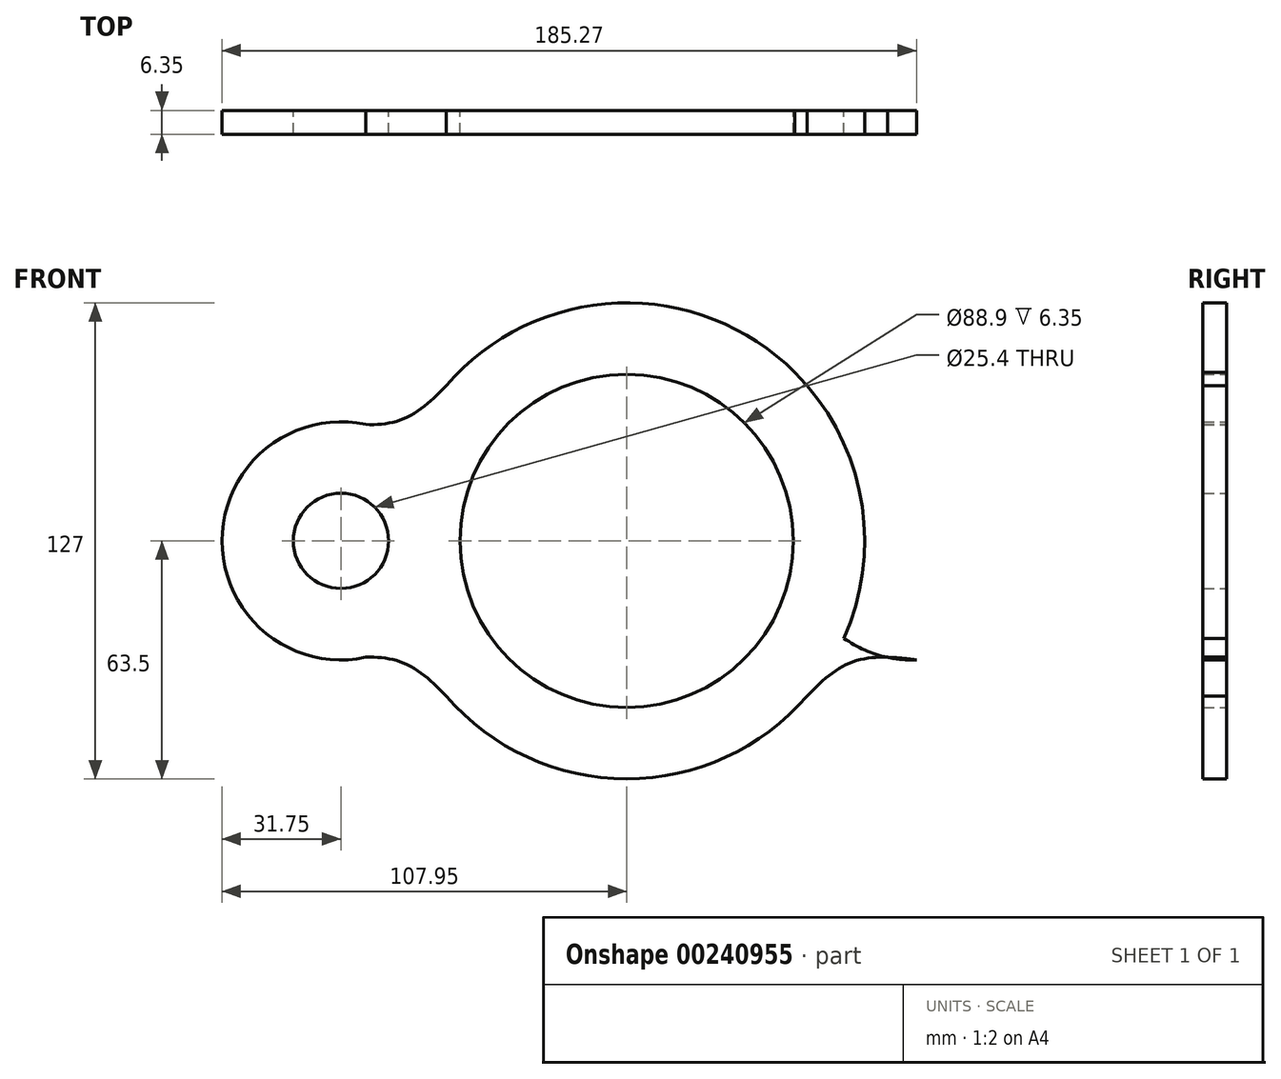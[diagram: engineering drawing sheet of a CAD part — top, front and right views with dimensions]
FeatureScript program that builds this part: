
annotation { "Feature Type Name" : "Feature", "Feature Type Description" : "" }
export const myFeature = defineFeature(function(context is Context, id is Id, definition is map)
    precondition{}
    {
        {
            var Q0;
            Q0=qCreatedBy(makeId("Front.planeOp"),FACE);
            var sketch = newSketch(context, id + "F0", { "sketchPlane" : qUnion([Q0])});
            skArc(sketch, "E0", {"start": v(0, 63.5) * mm, "mid": v(-44.9, 44.9) * mm, "end": v(-63.5, 0) * mm});
            skArc(sketch, "E1", {"start": v(-57.94, 25.98) * mm, "mid": v(-90.84, 28.18) * mm, "end": v(-107.95, 0) * mm});
            skFitSpline(sketch, "E2", {"points": [v(-44.9, 44.9) * mm, v(-60.08, 32.34) * mm, v(-77.32, 31.73) * mm], "startDerivative": vector(-27.75, -30.26) * mm, "endDerivative": vector(-37.2, 4.24) * mm});
            skFitSpline(sketch, "E3.MirrorCS", {"points": [v(-44.9, -44.9) * mm, v(-60.08, -32.34) * mm, v(-77.32, -31.73) * mm], "startDerivative": vector(-27.75, 30.26) * mm, "endDerivative": vector(-37.2, -4.24) * mm});
            skArc(sketch, "E4.MirrorCS", {"start": v(0, -63.5) * mm, "mid": v(-44.9, -44.9) * mm, "end": v(-63.5, 0) * mm});
            skArc(sketch, "E5.MirrorCS", {"start": v(-57.94, -25.98) * mm, "mid": v(-90.84, -28.18) * mm, "end": v(-107.95, 0) * mm});
            skArc(sketch, "E6.MirrorCS", {"start": v(0, 63.5) * mm, "mid": v(44.9, 44.9) * mm, "end": v(63.5, 0) * mm});
            skArc(sketch, "E7.MirrorCS", {"start": v(0, -63.5) * mm, "mid": v(44.9, -44.9) * mm, "end": v(63.5, 0) * mm});
            skArc(sketch, "E8.MirrorCS", {"start": v(57.94, -25.98) * mm, "mid": v(90.84, -28.18) * mm, "end": v(107.95, 0) * mm});
            skArc(sketch, "E9.MirrorCS", {"start": v(57.94, 25.98) * mm, "mid": v(90.84, 28.18) * mm, "end": v(107.95, 0) * mm});
            skFitSpline(sketch, "E10.MirrorCS", {"points": [v(44.9, 44.9) * mm, v(60.08, 32.34) * mm, v(77.32, 31.73) * mm], "startDerivative": vector(27.75, -30.26) * mm, "endDerivative": vector(37.2, 4.24) * mm});
            skFitSpline(sketch, "E11.MirrorCS", {"points": [v(44.9, -44.9) * mm, v(60.08, -32.34) * mm, v(77.32, -31.73) * mm], "startDerivative": vector(27.75, 30.26) * mm, "endDerivative": vector(37.2, -4.24) * mm});
            skCircle(sketch, "E12", {"center": v(0, 0) * mm, "radius": 44.45 * mm});
            skSolve(sketch);
        }
        {
            var Q0;
            {var subQ5=sQuery(id+"F0.wireOp",EDGE,"E7.MirrorCS");var subQ8=sQuery(id+"F0.wireOp",EDGE,"E6.MirrorCS");var subQ9=makeQuery(id+"F0.imprint","INTERSECT",VERTEX,{"derivedFrom":[subQ8,subQ5]});Q0=makeQuery(id+"F0.imprint","IMPRINT",FACE,{"disambiguationData":[TD([[makeQuery(id+"F0.imprint","IMPRINT",EDGE,{"disambiguationData":[TD([[subQ9,1.0]])],"derivedFrom":subQ8}),1.0]])]});}
            var Q1;
            {var subQ0=sQuery(id+"F0.wireOp",EDGE,"E4.MirrorCS");var subQ1=sQuery(id+"F0.wireOp",EDGE,"E3.MirrorCS");var subQ2=makeQuery(id+"F0.imprint","INTERSECT",VERTEX,{"disambiguationData":[OD(1.0)],"derivedFrom":[subQ1,subQ0]});Q1=makeQuery(id+"F0.imprint","IMPRINT",FACE,{"disambiguationData":[TD([[makeQuery(id+"F0.imprint","IMPRINT",EDGE,{"disambiguationData":[TD([[subQ2,-1.0]])],"derivedFrom":subQ1}),-1.0]])]});}
            var Q2;
            Q2=makeQuery(id+"F0.imprint","IMPRINT",FACE,{"disambiguationData":[TD([[makeQuery(id+"F0.imprint","IMPRINT",EDGE,{"derivedFrom":sQuery(id+"F0.wireOp",EDGE,"E12")}),1.0]])]});
            var Q3;
            {var subQ0=sQuery(id+"F0.wireOp",EDGE,"E9.MirrorCS");var subQ1=sQuery(id+"F0.wireOp",EDGE,"E6.MirrorCS");var subQ2=makeQuery(id+"F0.imprint","INTERSECT",VERTEX,{"derivedFrom":[subQ1,subQ0]});Q3=makeQuery(id+"F0.imprint","IMPRINT",FACE,{"disambiguationData":[TD([[makeQuery(id+"F0.imprint","IMPRINT",EDGE,{"disambiguationData":[TD([[subQ2,1.0]])],"derivedFrom":subQ1}),1.0]])]});}
            var Q4;
            {var subQ0=sQuery(id+"F0.wireOp",EDGE,"E8.MirrorCS");var subQ1=sQuery(id+"F0.wireOp",EDGE,"E7.MirrorCS");var subQ2=makeQuery(id+"F0.imprint","INTERSECT",VERTEX,{"derivedFrom":[subQ1,subQ0]});Q4=makeQuery(id+"F0.imprint","IMPRINT",FACE,{"disambiguationData":[TD([[makeQuery(id+"F0.imprint","IMPRINT",EDGE,{"disambiguationData":[TD([[subQ2,1.0]])],"derivedFrom":subQ1}),-1.0]])]});}
            var Q5;
            {var subQ0=sQuery(id+"F0.wireOp",EDGE,"E10.MirrorCS");var subQ1=sQuery(id+"F0.wireOp",EDGE,"E9.MirrorCS");var subQ2=makeQuery(id+"F0.imprint","INTERSECT",VERTEX,{"disambiguationData":[OD(0.0)],"derivedFrom":[subQ1,subQ0]});Q5=makeQuery(id+"F0.imprint","IMPRINT",FACE,{"disambiguationData":[TD([[makeQuery(id+"F0.imprint","IMPRINT",EDGE,{"disambiguationData":[TD([[subQ2,1.0]])],"derivedFrom":subQ1}),-1.0]])]});}
            var Q6;
            {var subQ0=sQuery(id+"F0.wireOp",EDGE,"E1");var subQ1=sQuery(id+"F0.wireOp",EDGE,"E0");var subQ2=makeQuery(id+"F0.imprint","INTERSECT",VERTEX,{"derivedFrom":[subQ1,subQ0]});Q6=makeQuery(id+"F0.imprint","IMPRINT",FACE,{"disambiguationData":[TD([[makeQuery(id+"F0.imprint","IMPRINT",EDGE,{"disambiguationData":[TD([[subQ2,1.0]])],"derivedFrom":subQ1}),-1.0]])]});}
            var Q7;
            {var subQ0=sQuery(id+"F0.wireOp",EDGE,"E5.MirrorCS");var subQ1=sQuery(id+"F0.wireOp",EDGE,"E3.MirrorCS");var subQ2=makeQuery(id+"F0.imprint","INTERSECT",VERTEX,{"disambiguationData":[OD(0.0)],"derivedFrom":[subQ1,subQ0]});Q7=makeQuery(id+"F0.imprint","IMPRINT",FACE,{"disambiguationData":[TD([[makeQuery(id+"F0.imprint","IMPRINT",EDGE,{"disambiguationData":[TD([[subQ2,1.0]])],"derivedFrom":subQ1}),1.0]])]});}
            var Q8;
            {var subQ0=sQuery(id+"F0.wireOp",EDGE,"E2");var subQ1=sQuery(id+"F0.wireOp",EDGE,"E0");var subQ2=makeQuery(id+"F0.imprint","INTERSECT",VERTEX,{"disambiguationData":[OD(0.0)],"derivedFrom":[subQ1,subQ0]});Q8=makeQuery(id+"F0.imprint","IMPRINT",FACE,{"disambiguationData":[TD([[makeQuery(id+"F0.imprint","IMPRINT",EDGE,{"disambiguationData":[TD([[subQ2,-1.0]])],"derivedFrom":subQ1}),1.0]])]});}
            var Q9;
            {var subQ0=sQuery(id+"F0.wireOp",EDGE,"E2");var subQ1=sQuery(id+"F0.wireOp",EDGE,"E1");var subQ2=makeQuery(id+"F0.imprint","INTERSECT",VERTEX,{"disambiguationData":[OD(0.0)],"derivedFrom":[subQ1,subQ0]});Q9=makeQuery(id+"F0.imprint","IMPRINT",FACE,{"disambiguationData":[TD([[makeQuery(id+"F0.imprint","IMPRINT",EDGE,{"disambiguationData":[TD([[subQ2,1.0]])],"derivedFrom":subQ1}),1.0]])]});}
            var Q10;
            {var subQ0=sQuery(id+"F0.wireOp",EDGE,"E11.MirrorCS");var subQ1=sQuery(id+"F0.wireOp",EDGE,"E7.MirrorCS");var subQ2=makeQuery(id+"F0.imprint","INTERSECT",VERTEX,{"disambiguationData":[OD(0.0)],"derivedFrom":[subQ1,subQ0]});Q10=makeQuery(id+"F0.imprint","IMPRINT",FACE,{"disambiguationData":[TD([[makeQuery(id+"F0.imprint","IMPRINT",EDGE,{"disambiguationData":[TD([[subQ2,-1.0]])],"derivedFrom":subQ1}),1.0]])]});}
            var Q11;
            {var subQ0=sQuery(id+"F0.wireOp",EDGE,"E10.MirrorCS");var subQ1=sQuery(id+"F0.wireOp",EDGE,"E6.MirrorCS");var subQ2=makeQuery(id+"F0.imprint","INTERSECT",VERTEX,{"disambiguationData":[OD(0.0)],"derivedFrom":[subQ1,subQ0]});Q11=makeQuery(id+"F0.imprint","IMPRINT",FACE,{"disambiguationData":[TD([[makeQuery(id+"F0.imprint","IMPRINT",EDGE,{"disambiguationData":[TD([[subQ2,-1.0]])],"derivedFrom":subQ1}),-1.0]])]});}
            var Q12;
            {var subQ0=sQuery(id+"F0.wireOp",EDGE,"E4.MirrorCS");var subQ1=sQuery(id+"F0.wireOp",EDGE,"E3.MirrorCS");var subQ2=makeQuery(id+"F0.imprint","INTERSECT",VERTEX,{"disambiguationData":[OD(0.0)],"derivedFrom":[subQ1,subQ0]});Q12=makeQuery(id+"F0.imprint","IMPRINT",FACE,{"disambiguationData":[TD([[makeQuery(id+"F0.imprint","IMPRINT",EDGE,{"disambiguationData":[TD([[subQ2,-1.0]])],"derivedFrom":subQ1}),1.0]])]});}
            var Q13;
            {var subQ0=sQuery(id+"F0.wireOp",EDGE,"E11.MirrorCS");var subQ1=sQuery(id+"F0.wireOp",EDGE,"E8.MirrorCS");var subQ2=makeQuery(id+"F0.imprint","INTERSECT",VERTEX,{"disambiguationData":[OD(0.0)],"derivedFrom":[subQ1,subQ0]});Q13=makeQuery(id+"F0.imprint","IMPRINT",FACE,{"disambiguationData":[TD([[makeQuery(id+"F0.imprint","IMPRINT",EDGE,{"disambiguationData":[TD([[subQ2,1.0]])],"derivedFrom":subQ1}),1.0]])]});}
            var Q14;
            Q14=makeQuery(id+"F0.imprint","IMPRINT",FACE,{"disambiguationData":[TD([[makeQuery(id+"F0.imprint","IMPRINT",EDGE,{"derivedFrom":sQuery(id+"F0.wireOp",EDGE,"E12")}),-1.0]])]});
            var Q15;
            {var subQ6=sQuery(id+"F0.wireOp",EDGE,"E4.MirrorCS");var subQ10=sQuery(id+"F0.wireOp",EDGE,"E0");var subQ12=makeQuery(id+"F0.imprint","INTERSECT",VERTEX,{"derivedFrom":[subQ10,subQ6]});Q15=makeQuery(id+"F0.imprint","IMPRINT",FACE,{"disambiguationData":[TD([[makeQuery(id+"F0.imprint","IMPRINT",EDGE,{"disambiguationData":[TD([[subQ12,1.0]])],"derivedFrom":subQ10}),-1.0]])]});}
            extrude(context, id + "F1", {"entities" : qUnion([Q0, Q1, Q2, Q3, Q4, Q5, Q6, Q7, Q8, Q9, Q10, Q11, Q12, Q13, Q14, Q15]), "depth" : 6.35 * mm});
        }
        {
            var Q0;
            Q0=qCreatedBy(makeId("Front.planeOp"),FACE);
            var sketch = newSketch(context, id + "F2", { "sketchPlane" : qUnion([Q0])});
            skCircle(sketch, "E13", {"center": v(0, 0) * mm, "radius": 44.45 * mm});
            skSolve(sketch);
        }
        {
            var Q0;
            Q0=sQuery(id+"F2.wireOp",VERTEX,"E13.center");
            var Q1;
            Q1=makeQuery(id+"F1.opExtrude","SWEPT_BODY",BODY,{"disambiguationData":[OSD([sQuery(id+"F0.wireOp",EDGE,"E0"),sQuery(id+"F0.wireOp",EDGE,"E1"),sQuery(id+"F0.wireOp",EDGE,"E2"),sQuery(id+"F0.wireOp",EDGE,"E3.MirrorCS"),sQuery(id+"F0.wireOp",EDGE,"E4.MirrorCS"),sQuery(id+"F0.wireOp",EDGE,"E5.MirrorCS"),sQuery(id+"F0.wireOp",EDGE,"E6.MirrorCS"),sQuery(id+"F0.wireOp",EDGE,"E7.MirrorCS"),sQuery(id+"F0.wireOp",EDGE,"E8.MirrorCS"),sQuery(id+"F0.wireOp",EDGE,"E9.MirrorCS"),sQuery(id+"F0.wireOp",EDGE,"E10.MirrorCS"),sQuery(id+"F0.wireOp",EDGE,"E11.MirrorCS")])]});
            hole(context, id + "F3", {"style" : HoleStyle.SIMPLE, "endStyle" : HoleEndStyle.THROUGH, "oppositeDirection" : true, "holeDiameter" : 88.9 * mm, "locations" : qUnion([Q0]), "scope" : qUnion([Q1]), "isTappedThrough" : true});
        }
        {
            var Q0;
            Q0=qCreatedBy(makeId("Front.planeOp"),FACE);
            var sketch = newSketch(context, id + "F4", { "sketchPlane" : qUnion([Q0])});
            skCircle(sketch, "E14", {"center": v(-76.2, 0) * mm, "radius": 12.7 * mm});
            skCircle(sketch, "E15", {"center": v(76.2, 0) * mm, "radius": 12.7 * mm});
            skSolve(sketch);
        }
        {
            var Q0;
            Q0=sQuery(id+"F4.wireOp",VERTEX,"E14.center");
            var Q1;
            Q1=sQuery(id+"F4.wireOp",VERTEX,"E15.center");
            var Q2;
            Q2=makeQuery(id+"F1.opExtrude","SWEPT_BODY",BODY,{"disambiguationData":[OSD([sQuery(id+"F0.wireOp",EDGE,"E0"),sQuery(id+"F0.wireOp",EDGE,"E1"),sQuery(id+"F0.wireOp",EDGE,"E2"),sQuery(id+"F0.wireOp",EDGE,"E3.MirrorCS"),sQuery(id+"F0.wireOp",EDGE,"E4.MirrorCS"),sQuery(id+"F0.wireOp",EDGE,"E5.MirrorCS"),sQuery(id+"F0.wireOp",EDGE,"E6.MirrorCS"),sQuery(id+"F0.wireOp",EDGE,"E7.MirrorCS"),sQuery(id+"F0.wireOp",EDGE,"E8.MirrorCS"),sQuery(id+"F0.wireOp",EDGE,"E9.MirrorCS"),sQuery(id+"F0.wireOp",EDGE,"E10.MirrorCS"),sQuery(id+"F0.wireOp",EDGE,"E11.MirrorCS")])]});
            hole(context, id + "F5", {"style" : HoleStyle.SIMPLE, "endStyle" : HoleEndStyle.THROUGH, "oppositeDirection" : true, "holeDiameter" : 25.4 * mm, "locations" : qUnion([Q0, Q1]), "scope" : qUnion([Q2]), "isTappedThrough" : true});
        }
    });
